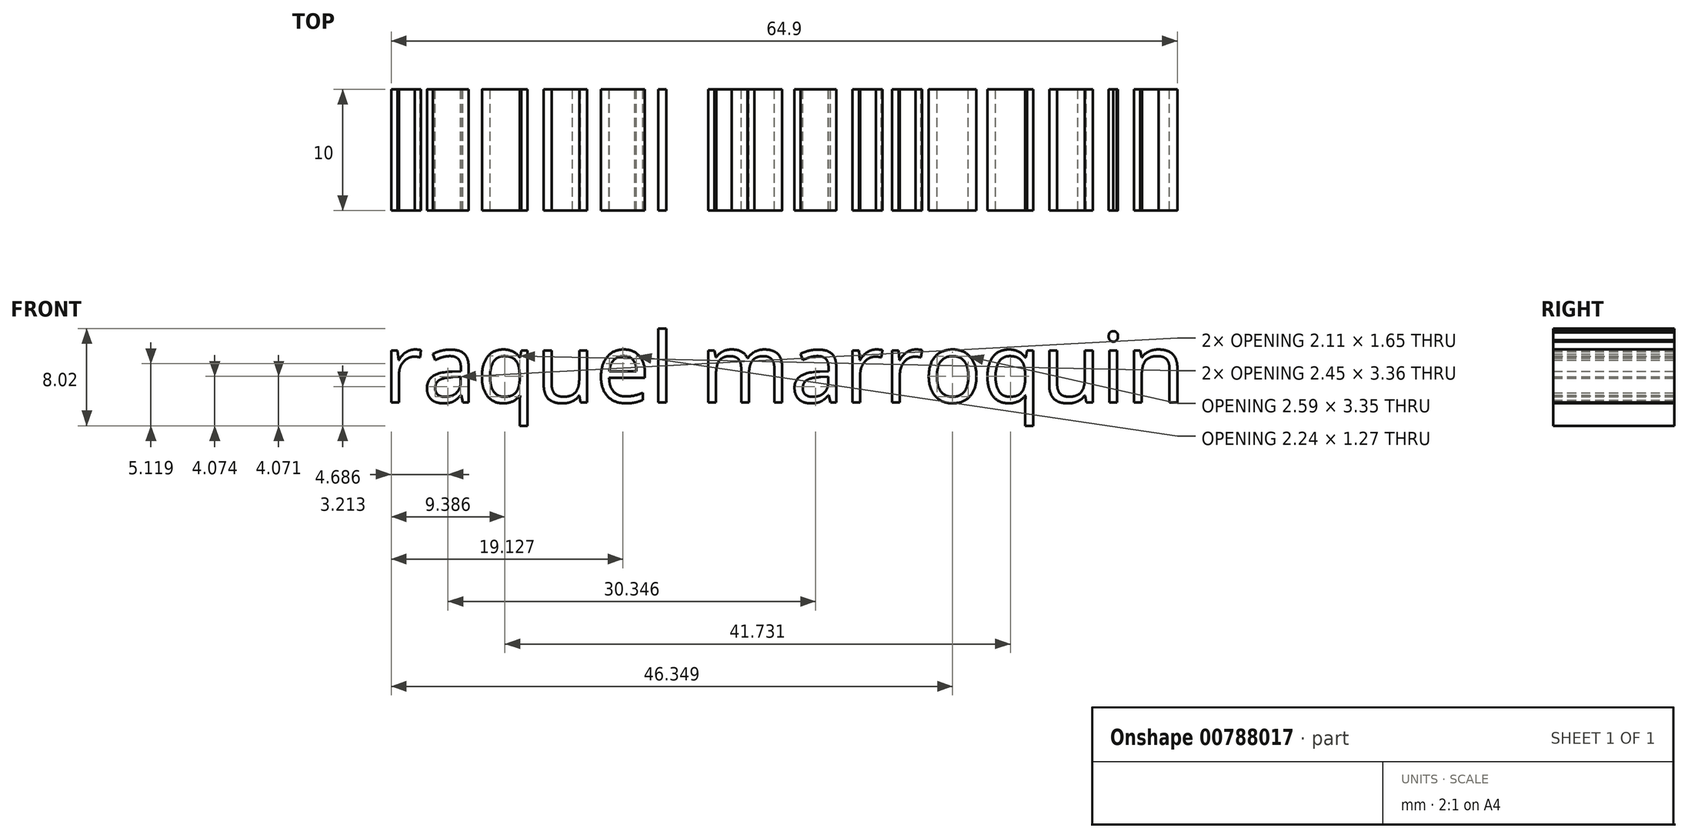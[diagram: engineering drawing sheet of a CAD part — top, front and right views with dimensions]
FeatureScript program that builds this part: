
annotation { "Feature Type Name" : "Feature", "Feature Type Description" : "" }
export const myFeature = defineFeature(function(context is Context, id is Id, definition is map)
    precondition{}
    {
        {
            var Q0;
            Q0=qCreatedBy(makeId("Front.planeOp"),FACE);
            var sketch = newSketch(context, id + "F0", { "sketchPlane" : qUnion([Q0])});
            skText(sketch, "E0", { "text": "raquel marroquin", "fontName": "OpenSans-Regular.ttf"});
            const initialGuessF0  = {"E0": [0, 0, 1, 0, 0.00577]};
            skSetInitialGuess(sketch, initialGuessF0);
            skSolve(sketch);
        }
        {
            var Q0;
            Q0 = qSketchRegion(id + "F0", true);
            extrude(context, id + "F1", {"entities" : qUnion([Q0]), "depth" : 10 * mm, "offsetDistance" : 25.4 * mm});
        }
    });
